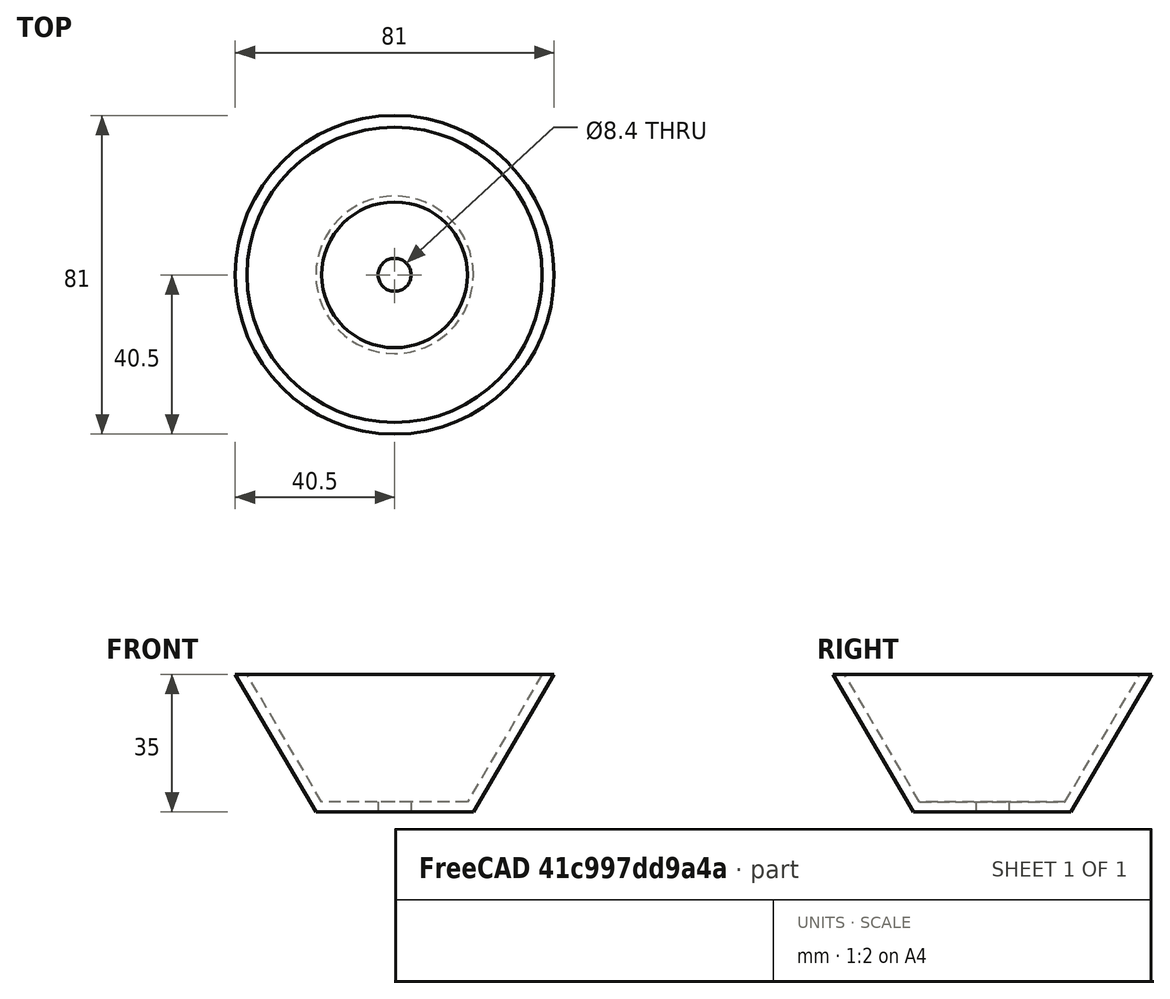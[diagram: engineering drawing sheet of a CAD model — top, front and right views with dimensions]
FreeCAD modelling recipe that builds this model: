
FCSTD DOCUMENT  (FreeCAD 0.19R24291 (Git))
Label: Для присосок
License: All rights reserved
LicenseURL: http://en.wikipedia.org/wiki/All_rights_reserved
objects: Sketcher::SketchObject×1, PartDesign::Revolution×1, PartDesign::Body×1
note: 4 computed .brp shape members not serialized (recipe doc carries the construction recipe); baked Part::Feature solids carry a one-line shape summary decoded from their .brp

FEATURE [Sketcher::SketchObject] Sketch
  FullyConstrained = true
  MapMode = 5
  Placement = pos=(0,0,0) rot=(1,0,0;1.5708rad)
  Support = -> [XZ_Plane]
  sketch-geometry (7):
    g0: LineSegment StartX=4.2 StartY=2.58865 StartZ=0 EndX=4.2 EndY=0 EndZ=0
    g1: LineSegment StartX=4.2 StartY=0 StartZ=0 EndX=20 EndY=0 EndZ=0
    g2: LineSegment StartX=20 StartY=0 StartZ=0 EndX=40.5 EndY=35 EndZ=0
    g3: LineSegment StartX=40.5 StartY=35 StartZ=0 EndX=37.5 EndY=35 EndZ=0
    g4: LineSegment StartX=37.5 StartY=35 StartZ=0 EndX=18.5162 EndY=2.58865 EndZ=0
    g5: LineSegment StartX=18.5162 StartY=2.58865 StartZ=0 EndX=4.2 EndY=2.58865 EndZ=0
    g6: LineSegment StartX=37.5 StartY=35 StartZ=0 EndX=39.7337 EndY=33.6917 EndZ=0
  constraints (23):
    c: PointOnObject(g0,g-1)
    c: Vertical(g0)
    c: Coincident(g1,g0)
    c: PointOnObject(g1,g-1)
    c: Coincident(g2,g1)
    c: Coincident(g3,g2)
    c: Horizontal(g3)
    c: Coincident(g4,g3)
    c: Coincident(g5,g4)
    c: Coincident(g5,g0)
    c: Horizontal(g5)
    c: Parallel(g4,g2)
    c: Distance(g2,g-1) = 35
    c: Distance(g1,g-2) = 20
    c: Distance(g0,g-2) = 4.2
    c: Distance(g3,g-2) = 37.5
    c: Distance(g2,g-2) = 40.5
    c: Coincident(g6,g3)
    c: PointOnObject(g6,g2)
    c: Perpendicular(g2,g6)
    c: Equal(g6,g0)
    c: Distance(g0) = 2.58865
    c: Angle(g2,g-1) = 2.10065
FEATURE [PartDesign::Revolution] Revolution
  Angle = 360
  Axis = (0,2e-16,1)
  Base = (0,0,0)
  Placement = pos=(0,0,0) rot=(1,0,0;1.5708rad)
  Profile = -> Sketch
  ReferenceAxis = -> Sketch [V_Axis]
  Reversed = true
FEATURE [PartDesign::Body] Body
  Group = -> [Sketch,Revolution]
  Origin = -> Origin
  Tip = -> Revolution
